# Revit family: Basin_Catch_24x24-Zurn-Z887-24-HD
name_source: partatom
category: Plumbing Fixtures
units: mm (PartAtom-declared; Revit-internal decimal feet)

## family parameters
Always vertical = Yes
Cut with Voids When Loaded = No
Maintain Annotation Orientation = No
OmniClass Number = 23.70.50.21.24.14
OmniClass Title = Deck Waste Water Drains
Part Type = Normal
Room Calculation Point = No
Round Connector Dimension = Use Radius
Shared = No
Work Plane-Based = No

## types (6) — shared parameters
Assembly Code = D2040300
CW Connection = No
Catch Basin Length = 24 "
Catch Basin Width = 22.75 "
Default Elevation = 1 "
Description = 23-1/4 [591] WIDE REVEAL X 24-5/8 [625] LONG CATCH BASIN WITH HEAVY DUTY FRAME
Grate = Ductile Iron - Zurn - Polished
HW Connection = No
Length = 24.625 "
Main Material = Polymer - Zurn - HDPE - Grey
Manufacturer = Zurn Water, LLC
Manufacurer Brand = Zurn
Modified Date = 12/29/2025
Product Documentation Link = https://files.zurn.com
Product Page URL = https://www.zurn.com
Product data url = https://bimobject.com
URL = www.zurn.com
Vent Connection = No
Waste Connection = Yes
Wide = 23.25 "
Width = 24 "
zero-valued in all types: CWFU, HWFU, WFU

## per-type parameters (varying)
| type | Actual Bottom Outlet (U) | Actual End Outlet (E) | Bottom Connector | Bottom Outlet (U) | End Connector | End Outlet (E) | Model | Nominal Bottom Outlet (U) | Nominal End Outlet (E) | Outlet Location | Outlet Radius | Product Installation Sheet URL |
| Z887-24-HD-3 Inch No-Hub Bottom Outlet | 3.5 " | 3.5 " | 1.5 " | Yes | 1.5 " | No | Z887-24-HD-U3 | 3 " | 3 " | 20.794 " | 1.75 " | https://files.zurn.com |
| Z887-24-HD-4 Inch No-Hub Bottom Outlet | 4.5 " | 4.5 " | 2 " | Yes | 2 " | No | Z887-24-HD-U4 | 4 " | 4 " | 20.794 " | 2.25 " |  |
| Z887-24-HD-6 Inch No-Hub Bottom Outlet | 6.625 " | 6.625 " | 3 " | Yes | 3 " | No | Z887-24-HD-U6 | 6 " | 6 " | 20.794 " | 3.313 " |  |
| Z887-24-HD-3 Inch No-Hub End Outlet | 3.5 " | 3.5 " | 1.5 " | No | 1.5 " | Yes | Z887-24-HD-E3 | 3 " | 3 " | 20.75 " | 1.75 " |  |
| Z887-24-HD-4 Inch No-Hub End Outlet | 4.5 " | 4.5 " | 2 " | No | 2 " | Yes | Z887-24-HD-E4 | 4 " | 4 " | 20.794 " | 2.25 " |  |
| Z887-24-HD-6 Inch No-Hub End Outlet | 6.625 " | 6.625 " | 3 " | No | 3 " | Yes | Z887-24-HD-E6 | 6 " | 6 " | 20.5 " | 3.313 " |  |

## geometry (parser evidence)
native form markers: Blend x4, Sweep x3
no freeform markers — native parametric forms only
